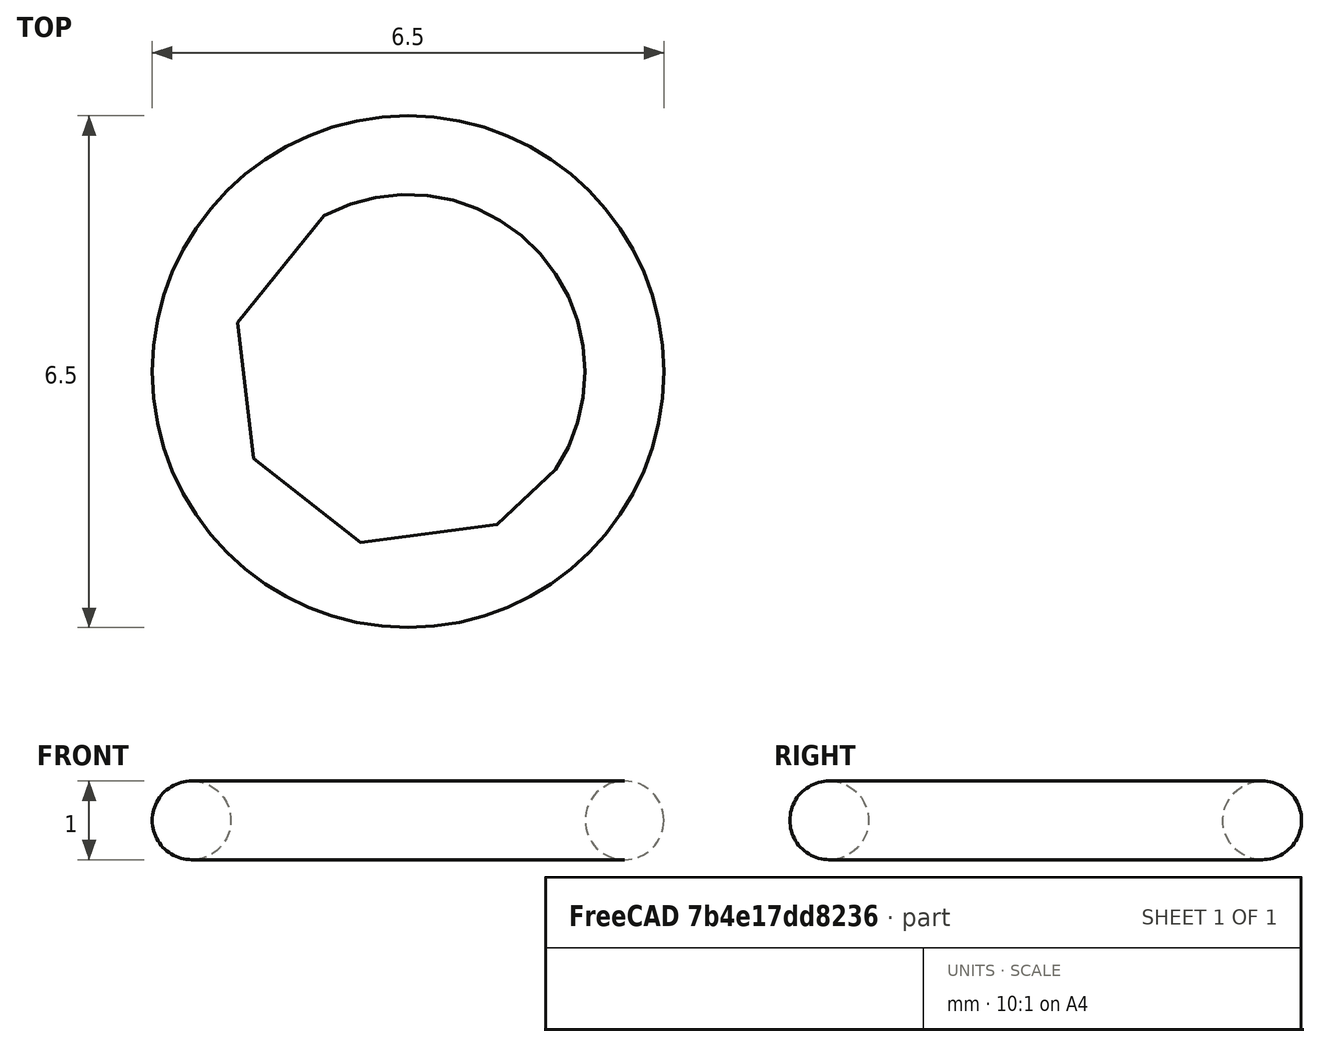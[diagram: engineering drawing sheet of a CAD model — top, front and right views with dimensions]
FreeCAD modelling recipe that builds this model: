
FCSTD DOCUMENT  (FreeCAD 0.21R33668 +26 (Git))
Label: O-Ring-actual
License: All rights reserved
LicenseURL: http://en.wikipedia.org/wiki/All_rights_reserved
objects: Sketcher::SketchObject×2, PartDesign::AdditivePipe×1, PartDesign::Body×1
note: 5 computed .brp shape members not serialized (recipe doc carries the construction recipe); baked Part::Feature solids carry a one-line shape summary decoded from their .brp

FEATURE [Sketcher::SketchObject] Sketch  label="path_oring_dia"
  FullyConstrained = true
  MapMode = 5
  Support = -> [XY_Plane]
  sketch-geometry (1):
    g0: Circle CenterX=0 CenterY=0 CenterZ=0 NormalX=0 NormalY=0 NormalZ=1 AngleXU=0 Radius=2.75
  constraints (2):
    c: Coincident(g0,g-1)
    c: Diameter(g0) = 5.5
FEATURE [Sketcher::SketchObject] Sketch001  label="pipe_thickness"
  FullyConstrained = true
  MapMode = 5
  Placement = pos=(0,0,0) rot=(1,0,0;1.5708rad)
  Support = -> [XZ_Plane]
  sketch-geometry (1):
    g0: Circle CenterX=2.75 CenterY=0 CenterZ=0 NormalX=0 NormalY=0 NormalZ=1 AngleXU=0 Radius=0.5
  constraints (3):
    c: PointOnObject(g0,g-1)
    c: DistanceX(g0) = 2.75
    c: Diameter(g0) = 1
FEATURE [PartDesign::AdditivePipe] AdditivePipe
  AuxilleryCurvelinear = true
  AuxillerySpineTangent = false
  Binormal = (0,0,0)
  Mode = 0
  Placement = pos=(0,0,0) rot=(1,0,0;1.5708rad)
  Profile = -> Sketch001
  Spine = -> Sketch [Edge1]
  SpineTangent = false
  Transformation = 0
  Transition = 0
FEATURE [PartDesign::Body] Body
  Group = -> [Sketch,Sketch001,AdditivePipe]
  Origin = -> Origin
  Tip = -> AdditivePipe
